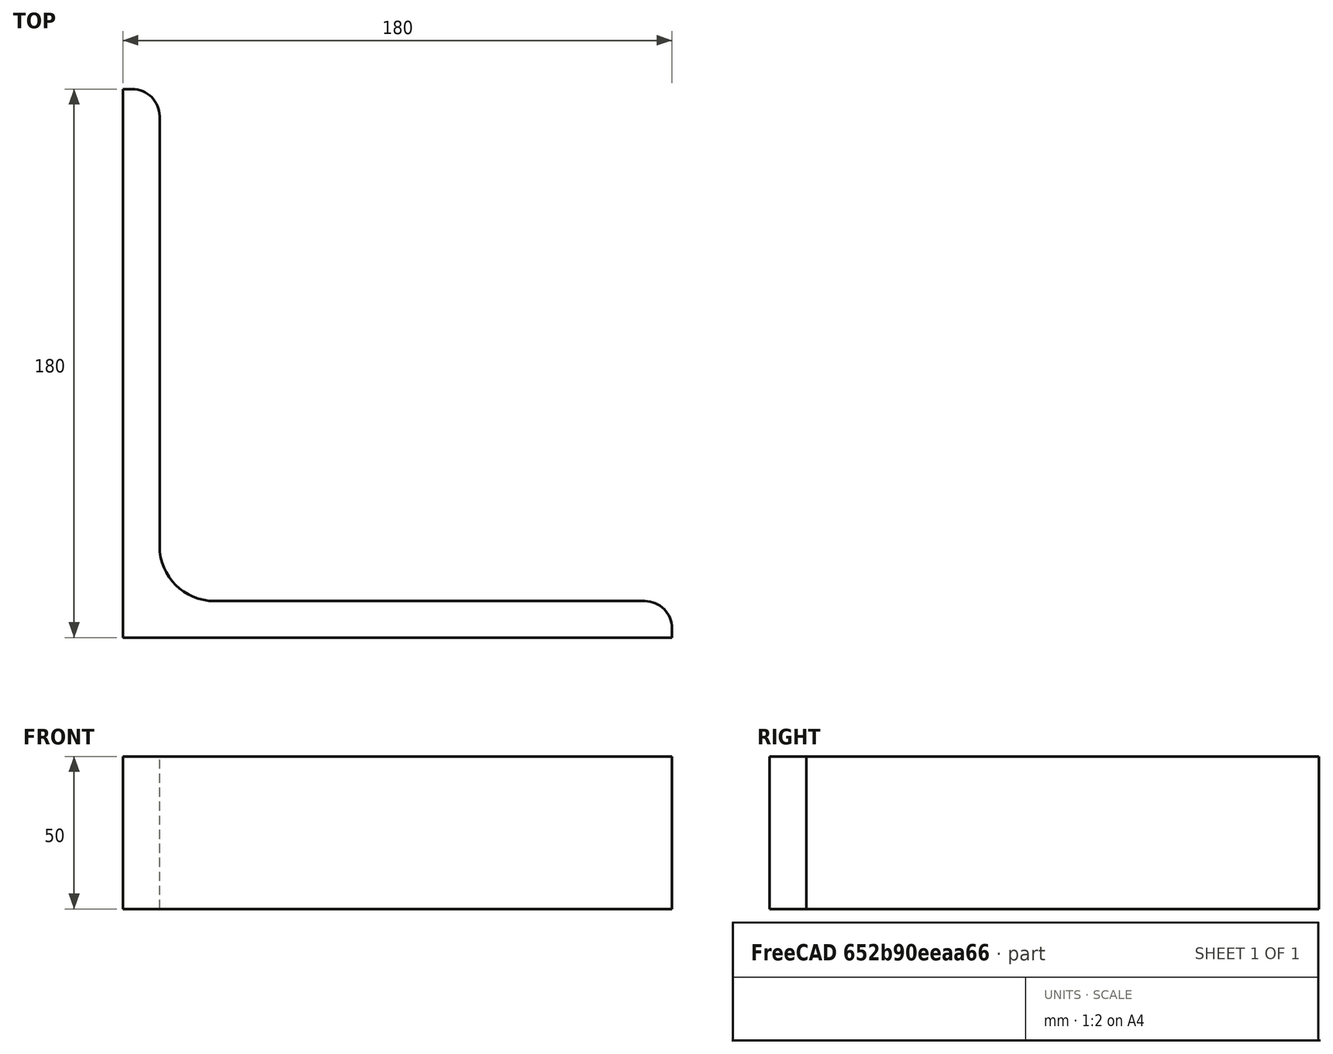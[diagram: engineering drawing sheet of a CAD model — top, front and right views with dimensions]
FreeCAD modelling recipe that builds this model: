
FCSTD DOCUMENT  (FreeCAD 0.15R4671 (Git))
Label: Angle Bar L180x180x12 EN10056 S235JR
License: All rights reserved
LicenseURL: http://en.wikipedia.org/wiki/All_rights_reserved
objects: Sketcher::SketchObject×1, Part::Extrusion×1
note: 2 computed .brp shape members not serialized (recipe doc carries the construction recipe); baked Part::Feature solids carry a one-line shape summary decoded from their .brp

FEATURE [Sketcher::SketchObject] Sketch
  sketch-geometry (9):
    g0: LineSegment StartX=0 StartY=0 StartZ=0 EndX=180 EndY=0 EndZ=0
    g1: LineSegment StartX=180 StartY=0 StartZ=0 EndX=180 EndY=3 EndZ=0
    g2: LineSegment StartX=171 StartY=12 StartZ=0 EndX=30 EndY=12 EndZ=0
    g3: LineSegment StartX=0 StartY=0 StartZ=0 EndX=0 EndY=180 EndZ=0
    g4: LineSegment StartX=0 StartY=180 StartZ=0 EndX=3 EndY=180 EndZ=0
    g5: LineSegment StartX=12 StartY=171 StartZ=0 EndX=12 EndY=30 EndZ=0
    g6: ArcOfCircle CenterX=30 CenterY=30 CenterZ=0 NormalX=0 NormalY=0 NormalZ=1 Radius=18 StartAngle=3.14159 EndAngle=4.71239
    g7: ArcOfCircle CenterX=3 CenterY=171 CenterZ=0 NormalX=0 NormalY=0 NormalZ=1 Radius=9 StartAngle=0 EndAngle=1.5708
    g8: ArcOfCircle CenterX=171 CenterY=3 CenterZ=0 NormalX=0 NormalY=0 NormalZ=1 Radius=9 StartAngle=0 EndAngle=1.5708
  constraints (23):
    c: Coincident(g0,g-1)
    c: Horizontal(g0)
    c: Coincident(g1,g0)
    c: Vertical(g1)
    c: Horizontal(g2)
    c: Coincident(g3,g-1)
    c: Vertical(g3)
    c: Coincident(g4,g3)
    c: Horizontal(g4)
    c: Vertical(g5)
    c: Tangent(g5,g6) = -1.5708
    c: Tangent(g2,g6) = 1.5708
    c: Tangent(g4,g7) = 1.5708
    c: Tangent(g5,g7) = 1.5708
    c: Tangent(g2,g8) = -1.5708
    c: Tangent(g1,g8) = -1.5708
    c: DistanceX(g0) = 180
    c: DistanceY(g3) = 180
    c: DistanceY(g0,g2) = 12
    c: DistanceX(g3,g5) = 12
    c: Radius(g6) = 18
    c: Radius(g8) = 9
    c: Radius(g7) = 9
FEATURE [Part::Extrusion] Extrude  label="Angle Bar L180x180x12 EN10056 S235JR"
  Base = -> Sketch
  Dir = (0,0,50)
  Solid = true
